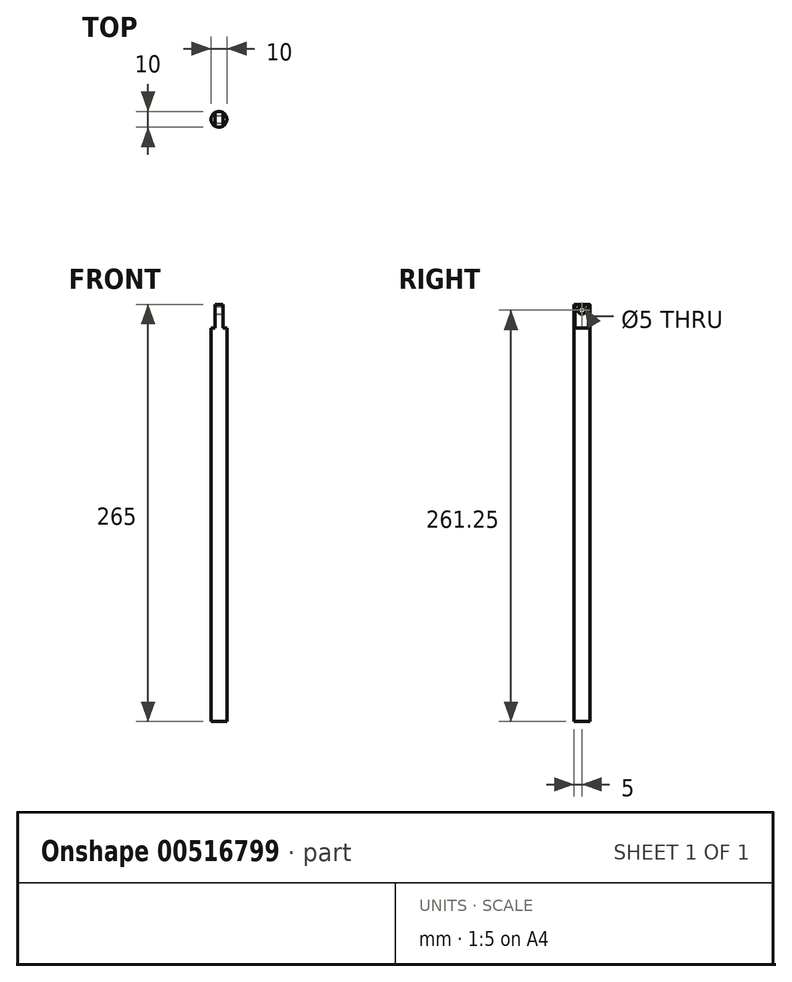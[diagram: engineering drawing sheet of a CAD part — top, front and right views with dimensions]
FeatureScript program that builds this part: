
annotation { "Feature Type Name" : "Feature", "Feature Type Description" : "" }
export const myFeature = defineFeature(function(context is Context, id is Id, definition is map)
    precondition{}
    {
        {
            var Q0;
            Q0=qCreatedBy(makeId("Front.planeOp"),FACE);
            var sketch = newSketch(context, id + "F0", { "sketchPlane" : qUnion([Q0])});
            skLineSegment(sketch, "E0", {"start": v(0, 0) * mm, "end": v(0, 250) * mm});
            skLineSegment(sketch, "E1", {"start": v(0, 250) * mm, "end": v(5, 250) * mm});
            skLineSegment(sketch, "E2", {"start": v(5, 250) * mm, "end": v(5, 0) * mm});
            skLineSegment(sketch, "E3", {"start": v(0, 0) * mm, "end": v(5, 0) * mm});
            skSolve(sketch);
        }
        {
            var Q0;
            Q0=makeQuery(id+"F0.imprint","IMPRINT",FACE,{"disambiguationData":[TD([[makeQuery(id+"F0.imprint","IMPRINT",EDGE,{"derivedFrom":sQuery(id+"F0.wireOp",EDGE,"E0")}),-1.0]])]});
            var Q1;
            Q1=sQuery(id+"F0.wireOp",EDGE,"E0");
            revolve(context, id + "F1", {"surfaceOperationType" : NewSurfaceOperationType.NEW, "entities" : qUnion([Q0]), "axis" : qUnion([Q1]), "revolveType" : RevolveType.FULL});
        }
        {
            var Q0;
            Q0=qCreatedBy(makeId("Front.planeOp"),FACE);
            var sketch = newSketch(context, id + "F2", { "sketchPlane" : qUnion([Q0])});
            skLineSegment(sketch, "E4", {"start": v(0, 250) * mm, "end": v(0, 265) * mm, "construction": true});
            skLineSegment(sketch, "E5", {"start": v(0, 265) * mm, "end": v(2.5, 265) * mm});
            skLineSegment(sketch, "E6", {"start": v(2.5, 265) * mm, "end": v(2.5, 250) * mm});
            skLineSegment(sketch, "E7", {"start": v(2.5, 250) * mm, "end": v(0, 250) * mm});
            skLineSegment(sketch, "E8", {"start": v(0, 265) * mm, "end": v(-2.5, 265) * mm});
            skLineSegment(sketch, "E9", {"start": v(-2.5, 265) * mm, "end": v(-2.5, 250) * mm});
            skLineSegment(sketch, "E10", {"start": v(-2.5, 250) * mm, "end": v(0, 250) * mm});
            skSolve(sketch);
        }
        {
            var Q0;
            Q0=makeQuery(id+"F2.imprint","IMPRINT",FACE,{"disambiguationData":[TD([[makeQuery(id+"F2.imprint","IMPRINT",EDGE,{"derivedFrom":sQuery(id+"F2.wireOp",EDGE,"E5")}),-1.0]])]});
            extrude(context, id + "F3", {"entities" : qUnion([Q0]), "operationType" : NewBodyOperationType.ADD, "oppositeDirection" : true, "depth" : 11.2 * mm, "offsetDistance" : 25 * mm, "symmetric" : true});
        }
        {
            var Q0;
            {var subQ0=sQuery(id+"F2.wireOp",EDGE,"E6");var subQ1=sQuery(id+"F2.wireOp",EDGE,"E10");var subQ2=sQuery(id+"F2.wireOp",EDGE,"E9");var subQ3=sQuery(id+"F2.wireOp",EDGE,"E7");Q0=makeQuery(id+"F3.boolean.opBoolean","SPLIT",FACE,{"disambiguationData":[TD([makeQuery(id+"F3.opExtrude","CAP_FACE",FACE,{"disambiguationData":[OSD([sQuery(id+"F2.wireOp",EDGE,"E5"),subQ0,subQ3,sQuery(id+"F2.wireOp",EDGE,"E8"),subQ2,subQ1])],"isStart":false})])],"derivedFrom":makeQuery(id+"F3.opExtrude","SWEPT_FACE",FACE,{"disambiguationData":[OSD([subQ3,subQ1])]})});}
            var Q1;
            {var subQ0=sQuery(id+"F2.wireOp",EDGE,"E6");var subQ1=sQuery(id+"F2.wireOp",EDGE,"E10");var subQ2=sQuery(id+"F2.wireOp",EDGE,"E9");var subQ3=sQuery(id+"F2.wireOp",EDGE,"E7");Q1=makeQuery(id+"F3.boolean.opBoolean","SPLIT",FACE,{"disambiguationData":[TD([makeQuery(id+"F3.opExtrude","CAP_FACE",FACE,{"disambiguationData":[OSD([sQuery(id+"F2.wireOp",EDGE,"E5"),subQ0,subQ3,sQuery(id+"F2.wireOp",EDGE,"E8"),subQ2,subQ1])],"isStart":true})])],"derivedFrom":makeQuery(id+"F3.opExtrude","SWEPT_FACE",FACE,{"disambiguationData":[OSD([subQ3,subQ1])]})});}
            extrude(context, id + "F4", {"entities" : qUnion([Q0, Q1]), "operationType" : NewBodyOperationType.REMOVE, "endBound" : BoundingType.THROUGH_ALL, "oppositeDirection" : true, "depth" : 25 * mm, "offsetDistance" : 25 * mm});
        }
        {
            var Q0;
            Q0=qCreatedBy(makeId("Right.planeOp"),FACE);
            var sketch = newSketch(context, id + "F5", { "sketchPlane" : qUnion([Q0])});
            skCircle(sketch, "E11", {"center": v(0, 261.25) * mm, "radius": 2.5 * mm});
            skSolve(sketch);
        }
        {
            var Q0;
            Q0 = qSketchRegion(id + "F5", true);
            extrude(context, id + "F6", {"entities" : qUnion([Q0]), "operationType" : NewBodyOperationType.REMOVE, "oppositeDirection" : true, "depth" : 25 * mm, "offsetDistance" : 25 * mm, "symmetric" : true});
        }
    });
